# Revit family: QF_BOURGEAT_Conteneurs_Isothermes_GN_pour_liquides
name_source: partatom
category: Equipement spécialisé
revit_build: Autodesk Revit 2015 (Build: 20140606_1530(x64)
units: mm (PartAtom-declared; Revit-internal decimal feet)

## types (6) — shared parameters
Certification = NF Hygiene alimentaire
Conception = En ployéthylène alimentaire
Fabricant = BOURGEAT
Nature isolant = Mousse sans PU
Spécification du Fabricant = Conteneur isotherme
URL catalogue = http://www.bourgeat.fr

## per-type parameters (varying)
| type | Capacité | Hauteur hors tout | Longueur hors tout | Modèle | Poids net à vide | Profondeur hors tout | Robinet |
| L5-avec robinet | 5 L | 370 mm  [stored 1.21391 ft] | 271 mm  [stored 0.889108 ft] | 825205 | 6.00 kg | 440 mm  [stored 1.44357 ft] | Oui |
| L17-avec robinet | 17 L | 437 mm  [stored 1.43373 ft] | 316 mm | 825217 | 10.00 kg | 604 mm  [stored 1.98163 ft] | Oui |
| L10-avec robinet | 10 L | 430 mm | 284 mm  [stored 0.931759 ft] | 825210 | 8.00 kg | 490 mm  [stored 1.60761 ft] | Oui |
| L5-sans robinet | 5 L | 370 mm  [stored 1.21391 ft] | 271 mm  [stored 0.889108 ft] | 825005 | 6.00 kg | 440 mm  [stored 1.44357 ft] | Non |
| L17-sans robinet | 17 L | 437 mm  [stored 1.43373 ft] | 316 mm | 825017 | 10.00 kg | 604 mm  [stored 1.98163 ft] | Non |
| L10-sans robinet | 10 L | 430 mm | 284 mm  [stored 0.931759 ft] | 825010 | 8.00 kg | 490 mm  [stored 1.60761 ft] | Non |

note: [stored X ft] marks values corroborated as IEEE doubles in the binary element streams (Revit-internal decimal feet)
